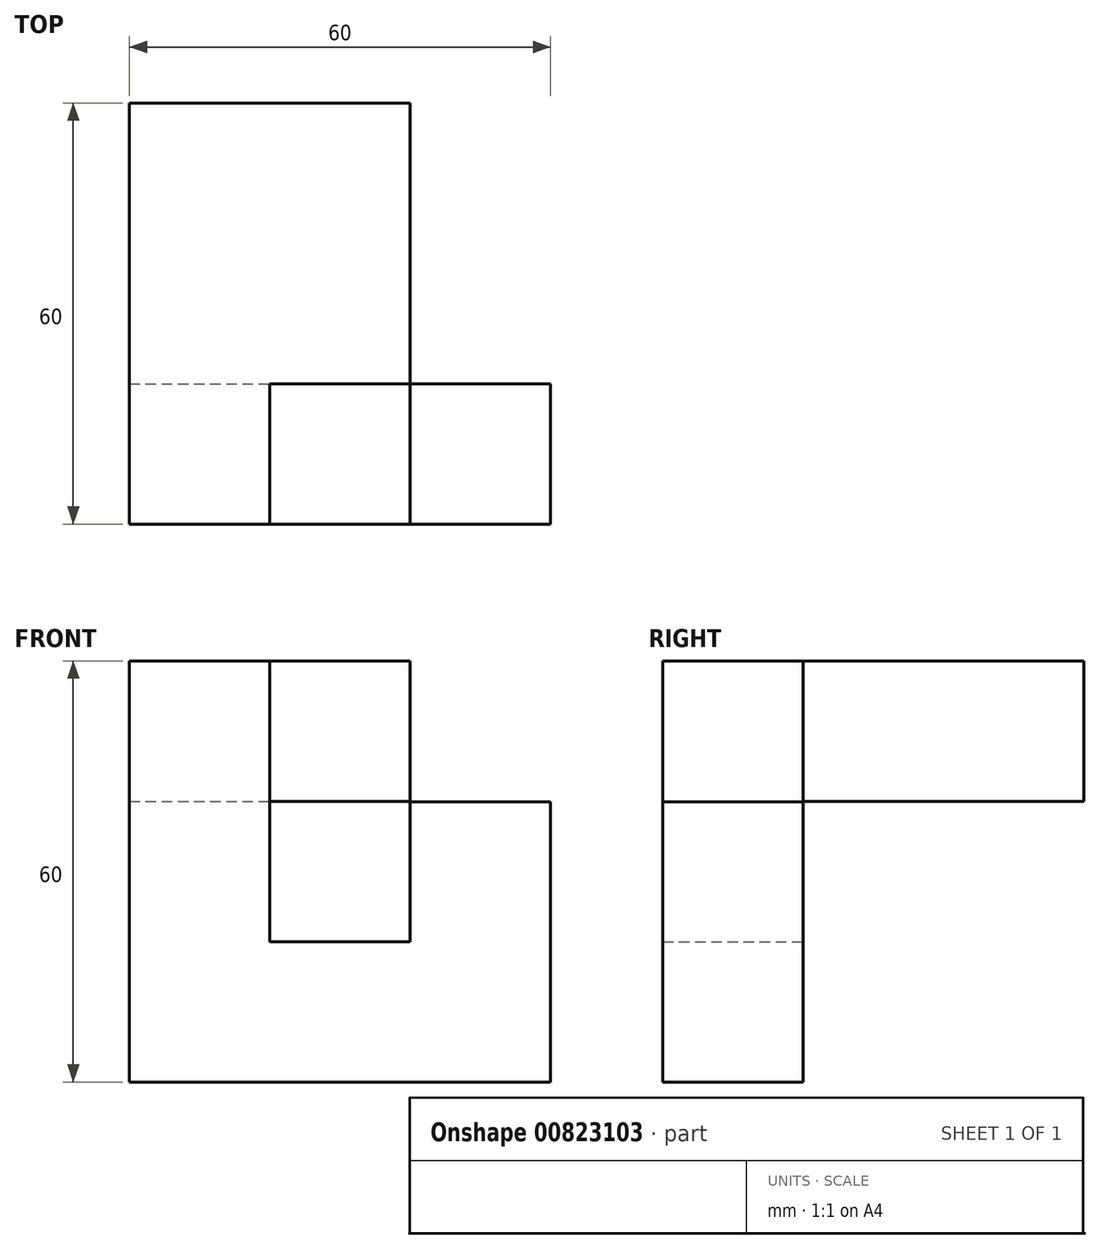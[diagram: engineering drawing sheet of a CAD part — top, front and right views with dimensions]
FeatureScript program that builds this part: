
annotation { "Feature Type Name" : "Feature", "Feature Type Description" : "" }
export const myFeature = defineFeature(function(context is Context, id is Id, definition is map)
    precondition{}
    {
        {
            var Q0;
            Q0=qCreatedBy(makeId("Front.planeOp"),FACE);
            var sketch = newSketch(context, id + "F0", { "sketchPlane" : qUnion([Q0])});
            skLineSegment(sketch, "E0.bottom", {"start": v(10, 10) * mm, "end": v(-10, 10) * mm});
            skLineSegment(sketch, "E0.top", {"start": v(10, -10) * mm, "end": v(-10, -10) * mm});
            skLineSegment(sketch, "E0.left", {"start": v(10, 10) * mm, "end": v(10, -10) * mm});
            skLineSegment(sketch, "E0.right", {"start": v(-10, 10) * mm, "end": v(-10, -10) * mm});
            skPoint(sketch, "E0.middle", {"position": v(0, 0) * mm});
            skSolve(sketch);
        }
        {
            var Q0;
            Q0 = qSketchRegion(id + "F0", true);
            extrude(context, id + "F1", {"entities" : qUnion([Q0]), "depth" : 60 * mm, "offsetDistance" : 25.4 * mm});
        }
        {
            var Q0;
            Q0=makeQuery(id+"F1.opExtrude","SWEPT_FACE",FACE,{"disambiguationData":[OSD([sQuery(id+"F0.wireOp",EDGE,"E0.left")])]});
            var sketch = newSketch(context, id + "F2", { "sketchPlane" : qUnion([Q0])});
            skLineSegment(sketch, "E1.bottom", {"start": v(0, -10) * mm, "end": v(-40, -10) * mm});
            skLineSegment(sketch, "E1.top", {"start": v(0, 10) * mm, "end": v(-40, 10) * mm});
            skLineSegment(sketch, "E1.left", {"start": v(0, -10) * mm, "end": v(0, 10) * mm});
            skLineSegment(sketch, "E1.right", {"start": v(-40, -10) * mm, "end": v(-40, 10) * mm});
            skSolve(sketch);
        }
        {
            var Q0;
            Q0 = qSketchRegion(id + "F2", true);
            extrude(context, id + "F3", {"entities" : qUnion([Q0]), "operationType" : NewBodyOperationType.ADD, "depth" : 20 * mm, "offsetDistance" : 25.4 * mm});
        }
        {
            var Q0;
            Q0=makeQuery(id+"F3.boolean.opBoolean","MERGE",FACE,{"derivedFrom":[makeQuery(id+"F1.opExtrude","SWEPT_FACE",FACE,{"disambiguationData":[OSD([sQuery(id+"F0.wireOp",EDGE,"E0.top")])]}),makeQuery(id+"F3.opExtrude","SWEPT_FACE",FACE,{"disambiguationData":[OSD([sQuery(id+"F2.wireOp",EDGE,"E1.bottom")])]})]});
            var sketch = newSketch(context, id + "F4", { "sketchPlane" : qUnion([Q0])});
            skLineSegment(sketch, "E2.bottom", {"start": v(-10, 60) * mm, "end": v(10, 60) * mm});
            skLineSegment(sketch, "E2.top", {"start": v(-10, 40) * mm, "end": v(10, 40) * mm});
            skLineSegment(sketch, "E2.left", {"start": v(-10, 60) * mm, "end": v(-10, 40) * mm});
            skLineSegment(sketch, "E2.right", {"start": v(10, 60) * mm, "end": v(10, 40) * mm});
            skSolve(sketch);
        }
        {
            var Q0;
            Q0 = qSketchRegion(id + "F4", true);
            extrude(context, id + "F5", {"entities" : qUnion([Q0]), "operationType" : NewBodyOperationType.ADD, "depth" : 40 * mm, "offsetDistance" : 25.4 * mm});
        }
        {
            var Q0;
            Q0=makeQuery(id+"F5.boolean.opBoolean","MERGE",FACE,{"derivedFrom":[makeQuery(id+"F1.opExtrude","SWEPT_FACE",FACE,{"disambiguationData":[OSD([sQuery(id+"F0.wireOp",EDGE,"E0.left")])]}),makeQuery(id+"F5.opExtrude","SWEPT_FACE",FACE,{"disambiguationData":[OSD([sQuery(id+"F4.wireOp",EDGE,"E2.right")])]})]});
            var sketch = newSketch(context, id + "F6", { "sketchPlane" : qUnion([Q0])});
            skLineSegment(sketch, "E3.bottom", {"start": v(-60, -50) * mm, "end": v(-40, -50) * mm});
            skLineSegment(sketch, "E3.top", {"start": v(-60, -30) * mm, "end": v(-40, -30) * mm});
            skLineSegment(sketch, "E3.left", {"start": v(-60, -50) * mm, "end": v(-60, -30) * mm});
            skLineSegment(sketch, "E3.right", {"start": v(-40, -50) * mm, "end": v(-40, -30) * mm});
            skSolve(sketch);
        }
        {
            var Q0;
            Q0 = qSketchRegion(id + "F6", true);
            extrude(context, id + "F7", {"entities" : qUnion([Q0]), "operationType" : NewBodyOperationType.ADD, "depth" : 40 * mm, "offsetDistance" : 25.4 * mm});
        }
        {
            var Q0;
            Q0=makeQuery(id+"F7.opExtrude","SWEPT_FACE",FACE,{"disambiguationData":[OSD([sQuery(id+"F6.wireOp",EDGE,"E3.top")])]});
            var sketch = newSketch(context, id + "F8", { "sketchPlane" : qUnion([Q0])});
            skLineSegment(sketch, "E4.bottom", {"start": v(50, -60) * mm, "end": v(30, -60) * mm});
            skLineSegment(sketch, "E4.top", {"start": v(50, -40) * mm, "end": v(30, -40) * mm});
            skLineSegment(sketch, "E4.left", {"start": v(50, -60) * mm, "end": v(50, -40) * mm});
            skLineSegment(sketch, "E4.right", {"start": v(30, -60) * mm, "end": v(30, -40) * mm});
            skSolve(sketch);
        }
        {
            var Q0;
            Q0 = qSketchRegion(id + "F8", true);
            extrude(context, id + "F9", {"entities" : qUnion([Q0]), "operationType" : NewBodyOperationType.ADD, "depth" : 19.9 * mm, "offsetDistance" : 25.4 * mm});
        }
    });
